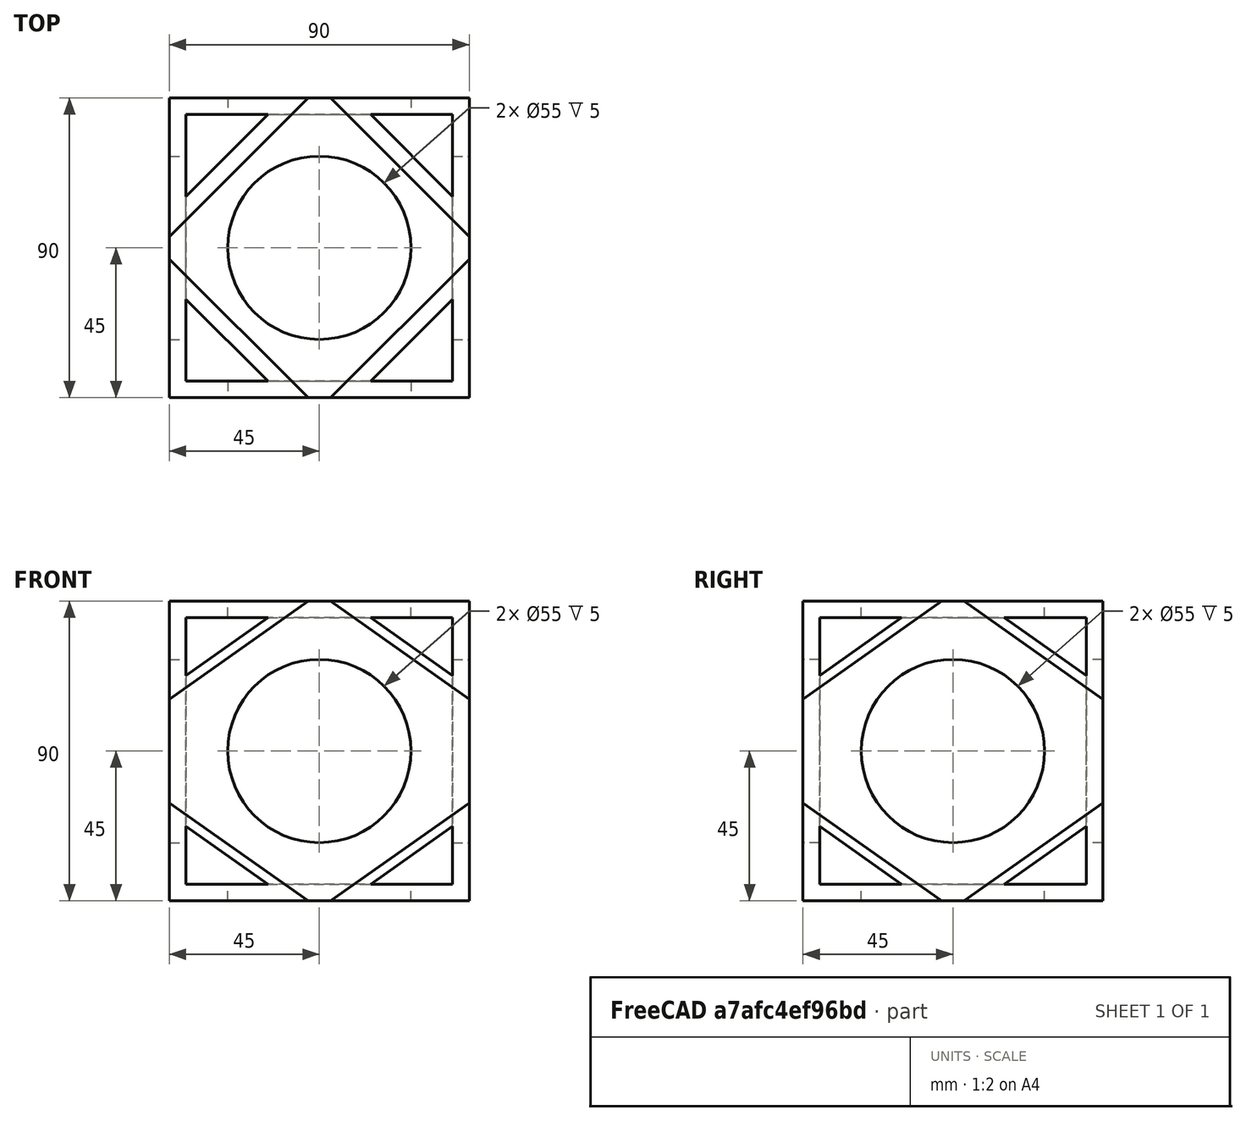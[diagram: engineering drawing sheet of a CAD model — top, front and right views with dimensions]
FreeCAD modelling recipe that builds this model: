
FCSTD DOCUMENT  (FreeCAD 0.16R6703 (Git))
Label: Tutorial_WhiffleBall
License: All rights reserved
LicenseURL: http://en.wikipedia.org/wiki/All_rights_reserved
objects: Part::Box×6, Part::Cut×5, Part::Cylinder×3, Part::MultiFuse×1
note: 15 computed .brp shape members not serialized (recipe doc carries the construction recipe); baked Part::Feature solids carry a one-line shape summary decoded from their .brp

FEATURE [Part::Box] Box  label="Cube"
  Height = 90
  Length = 90
  Placement = pos=(-45,-45,-45) rot=(0,0,1;0rad)
  Width = 90
FEATURE [Part::Box] Box001  label="Cube001"
  Height = 80
  Length = 80
  Placement = pos=(-40,-40,-40) rot=(0,0,1;0rad)
  Width = 80
FEATURE [Part::Cylinder] Cylinder
  Angle = 360
  Height = 120
  Placement = pos=(0,0,-60) rot=(0,0,1;0rad)
  Radius = 27.5
FEATURE [Part::Cylinder] Cylinder001
  Angle = 360
  Height = 120
  Placement = pos=(0,60,0) rot=(1,0,0;1.5708rad)
  Radius = 27.5
FEATURE [Part::Cylinder] Cylinder002
  Angle = 360
  Height = 120
  Placement = pos=(-60,0,0) rot=(0,1,0;1.5708rad)
  Radius = 27.5
FEATURE [Part::MultiFuse] Fusion
  Shapes = -> [Box001,Cylinder002,Cylinder001,Cylinder]
FEATURE [Part::Cut] Cut
  Base = -> Box
  Tool = -> Fusion
FEATURE [Part::Box] Box002  label="Cube002"
  Height = 112
  Length = 140
  Placement = pos=(-49.4975,-49.4975,-79.196) rot=(0.678598,0.281085,0.678598;1.09606rad)
  Width = 112
FEATURE [Part::Box] Box003  label="Cube003"
  Height = 180
  Length = 180
  Placement = pos=(-63.6396,-63.6396,-127.279) rot=(0.678598,0.281085,0.678598;1.09606rad)
  Width = 180
FEATURE [Part::Box] Box004  label="Cube004"
  Height = 112
  Length = 140
  Placement = pos=(-49.4975,49.4975,-79.196) rot=(0.678598,-0.281085,-0.678598;1.09606rad)
  Width = 112
FEATURE [Part::Box] Box005  label="Cube005"
  Height = 180
  Length = 180
  Placement = pos=(-63.6396,63.6396,-127.279) rot=(0.678598,-0.281085,-0.678598;1.09606rad)
  Width = 180
FEATURE [Part::Cut] Cut001
  Base = -> Box003
  Tool = -> Box002
FEATURE [Part::Cut] Cut002
  Base = -> Box005
  Tool = -> Box004
FEATURE [Part::Cut] Cut003
  Base = -> Cut
  Tool = -> Cut001
FEATURE [Part::Cut] Cut004
  Base = -> Cut003
  Tool = -> Cut002
